# Revit family: zzzShower_Set-GROHE-Europlus-350510001
name_source: partatom
category: Plumbing Fixtures
units: mm (PartAtom-declared; Revit-internal decimal feet)

## family parameters
Cut with Voids When Loaded = No
Host = Face
OmniClass Number = 23.45.05.14.17
OmniClass Title = Showers
Part Type = Normal
Room Calculation Point = No
Round Connector Dimension = Use Diameter
Shared = Yes

## types (1)
- 35051000
    19881000 Balance Trim = Yes
    26076002 Shower Slide Bar Kit = Yes
    26409000 Showerhead = Yes
    28577000 Shower Arm = Yes
    28672000 Shower Elbow = Yes
    35026000 Rough-In Box = Sold Separately
    ADA Compliant = Yes
    Assembly Code = D2010710
    CW Connection = Yes
    CWFU = 1.5
    CalGreen Compliant = Yes
    Default Elevation = 0"
    Description = EUROPLUS® Pressure Balance Valve Shower Set
    Diameter- Showerhead = 4 1/8"
    Finish = Metal-Grohe-000-StarLight Chrome
    Flow Rate = 1.75 GPM
    HW Connection = Yes
    HWFU = 1.5
    Installation Type = Wall Mounted
    Manufacturer = Grohe
    Material = Metal-Grohe-000-StarLight Chrome
    Model = 35051000
    Price = Prices may vary. Please consult Manufacturer Representative for most up-to-date price list.
    Product Documentation Link = https://americanstandard.box.com
    Product Page URL = https://www.grohe.us
    Revised Date = 01/11/2021
    Tempered Connection Diameter = 1/2"
    URL = https://www.grohe.us
    Vent Connection = No
    WFU = 2
    Waste Connection = No
    cUPC Compliant = Yes

## geometry (parser evidence)
native form markers: Sweep x15
no freeform markers — native parametric forms only
